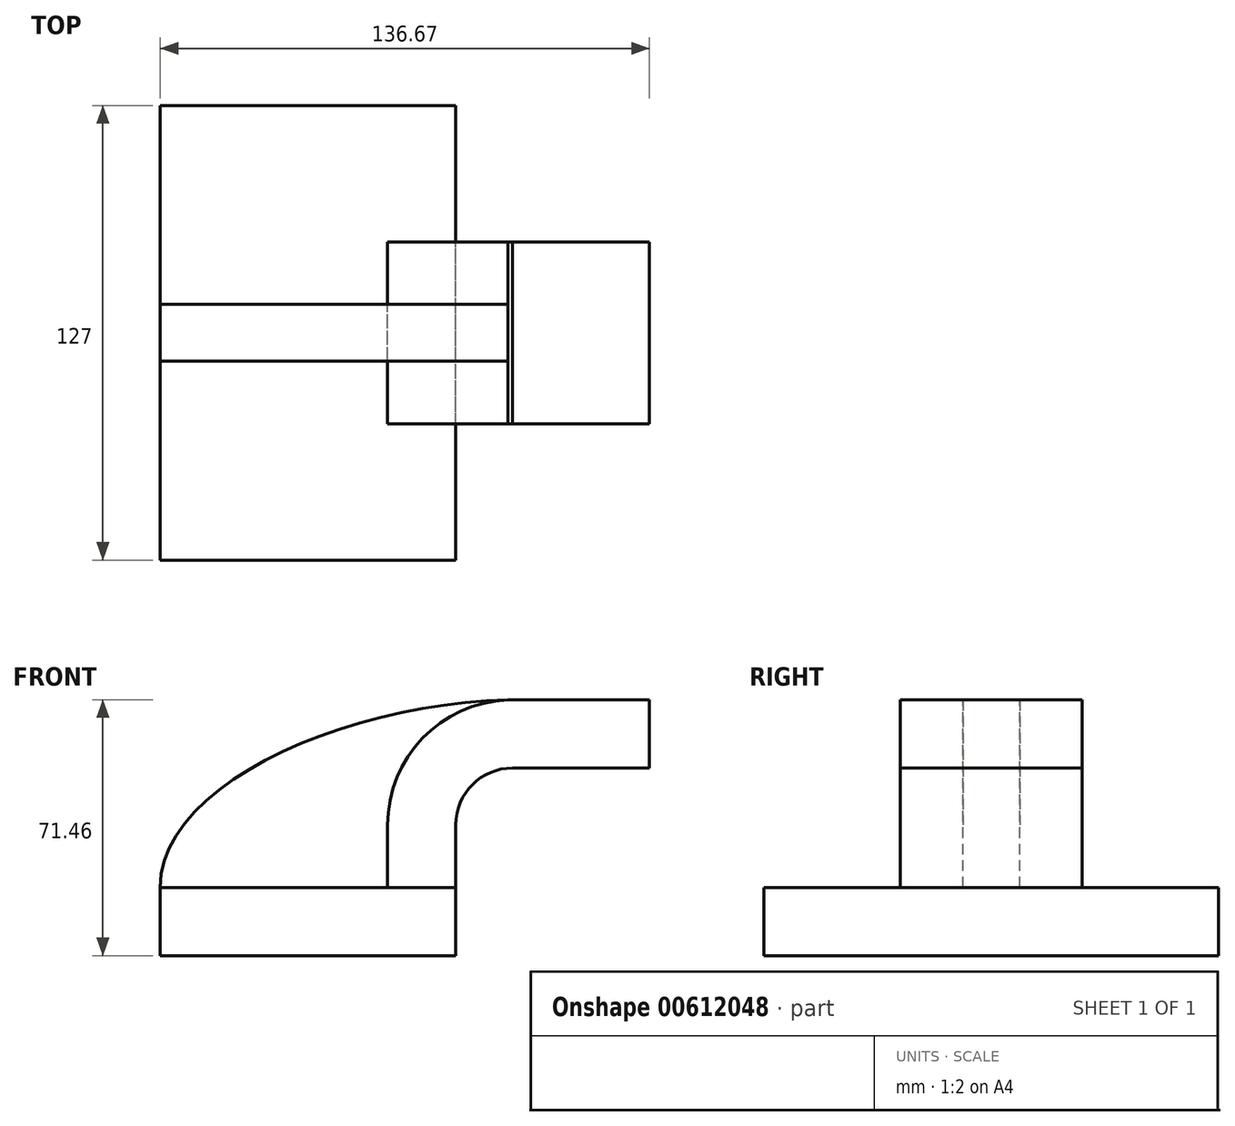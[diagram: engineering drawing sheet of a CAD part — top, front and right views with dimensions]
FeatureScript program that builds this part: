
annotation { "Feature Type Name" : "Feature", "Feature Type Description" : "" }
export const myFeature = defineFeature(function(context is Context, id is Id, definition is map)
    precondition{}
    {
        {
            var Q0;
            Q0=qCreatedBy(makeId("Front.planeOp"),FACE);
            var sketch = newSketch(context, id + "F0", { "sketchPlane" : qUnion([Q0])});
            skLineSegment(sketch, "E0.bottom", {"start": v(-41.28, 9.52) * mm, "end": v(41.27, 9.53) * mm});
            skLineSegment(sketch, "E0.top", {"start": v(-41.28, -9.53) * mm, "end": v(41.28, -9.53) * mm});
            skLineSegment(sketch, "E0.left", {"start": v(-41.28, 9.52) * mm, "end": v(-41.27, -9.53) * mm});
            skLineSegment(sketch, "E0.right", {"start": v(41.28, 9.53) * mm, "end": v(41.28, -9.52) * mm});
            skPoint(sketch, "E0.middle", {"position": v(0, 0) * mm});
            skLineSegment(sketch, "E1.bottom", {"start": v(60.32, 66.68) * mm, "end": v(111.12, 66.68) * mm});
            skLineSegment(sketch, "E1.top", {"start": v(60.32, 38.1) * mm, "end": v(111.12, 38.1) * mm});
            skLineSegment(sketch, "E1.left", {"start": v(60.32, 66.68) * mm, "end": v(60.32, 38.1) * mm});
            skLineSegment(sketch, "E1.right", {"start": v(111.12, 66.68) * mm, "end": v(111.12, 38.1) * mm});
            skPoint(sketch, "E1.middle", {"position": v(85.72, 52.39) * mm});
            skLineSegment(sketch, "E2", {"start": v(41.27, 9.53) * mm, "end": v(41.27, 27) * mm});
            skArc(sketch, "E3", {"start": v(41.27, 27) * mm, "mid": v(45.92, 38.23) * mm, "end": v(57.15, 42.88) * mm});
            skLineSegment(sketch, "E4", {"start": v(57.15, 42.88) * mm, "end": v(95.4, 42.88) * mm});
            skLineSegment(sketch, "E5.0", {"start": v(57.15, 61.93) * mm, "end": v(95.4, 61.93) * mm});
            skArc(sketch, "E5.1", {"start": v(22.22, 27) * mm, "mid": v(32.45, 51.7) * mm, "end": v(57.15, 61.93) * mm});
            skLineSegment(sketch, "E5.2", {"start": v(22.22, 9.53) * mm, "end": v(22.22, 27) * mm});
            skLineSegment(sketch, "E6", {"start": v(95.4, 42.88) * mm, "end": v(95.4, 61.93) * mm});
            skFitSpline(sketch, "E7", {"points": [v(-41.28, 9.52) * mm, v(57.15, 61.93) * mm], "startDerivative": vector(0.12, 88.14) * mm, "endDerivative": vector(135.8, 1.96) * mm});
            skSolve(sketch);
        }
        {
            var Q0;
            Q0=makeQuery(id+"F0.imprint","IMPRINT",FACE,{"disambiguationData":[TD([[makeQuery(id+"F0.imprint","IMPRINT",EDGE,{"derivedFrom":sQuery(id+"F0.wireOp",EDGE,"E0.top")}),1.0]])]});
            extrude(context, id + "F1", {"entities" : qUnion([Q0]), "endBound" : BoundingType.SYMMETRIC, "depth" : 127 * mm, "offsetDistance" : 25.4 * mm});
        }
        {
            var Q0;
            {var subQ1=sQuery(id+"F0.wireOp",EDGE,"E2");Q0=makeQuery(id+"F0.imprint","IMPRINT",FACE,{"disambiguationData":[TD([[makeQuery(id+"F0.imprint","IMPRINT",EDGE,{"derivedFrom":subQ1}),1.0]])]});}
            var Q1;
            {var subQ5=sQuery(id+"F0.wireOp",EDGE,"E6");Q1=makeQuery(id+"F0.imprint","IMPRINT",FACE,{"disambiguationData":[TD([[makeQuery(id+"F0.imprint","IMPRINT",EDGE,{"derivedFrom":subQ5}),1.0]])]});}
            extrude(context, id + "F2", {"entities" : qUnion([Q0, Q1]), "endBound" : BoundingType.SYMMETRIC, "depth" : 50.8 * mm, "offsetDistance" : 25.4 * mm});
        }
        {
            var Q0;
            {var subQ3=sQuery(id+"F0.wireOp",EDGE,"E5.2");Q0=makeQuery(id+"F0.imprint","IMPRINT",FACE,{"disambiguationData":[TD([[makeQuery(id+"F0.imprint","IMPRINT",EDGE,{"derivedFrom":subQ3}),1.0]])]});}
            extrude(context, id + "F3", {"entities" : qUnion([Q0]), "endBound" : BoundingType.SYMMETRIC, "depth" : 15.88 * mm, "offsetDistance" : 25.4 * mm});
        }
    });
